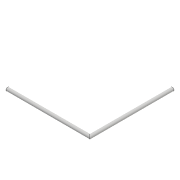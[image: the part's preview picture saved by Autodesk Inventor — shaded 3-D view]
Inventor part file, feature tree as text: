
AUTODESK INVENTOR PART (.ipt)
format: ipt  version: 2017 (Build 210142000, 142)  size: 75,264 bytes
history: native  units: mm
features: sketch x2, sweep x1
ambient origin geometry x8: Origin, YZ Plane, XZ Plane, XY Plane, X Axis, Y Axis, Z Axis, Center Point
bodies: Solid1 (feature_tree)
feature tree (3):
  sweep  "Sweep1"
  sketch  "Sketch1"  dims[d0=250.0mm d1=250.0mm]
  sketch  "Sketch2"  dims[d2=10.0mm d3=0.0mm d4=0.0mm]
